# Revit family: SOLID EXIT LED EMERGENCY EXIT LIGHT TWT3051WK
name_source: partatom
category: Lighting Fixtures
revit_build: Autodesk Revit 2015 (Build: 20160512_0715(x64)
units: mm (PartAtom-declared; Revit-internal decimal feet)

## types (4) — shared parameters
Color = RAL9003
Default Elevation = 1219 mm
Depth = 181 mm  [stored 0.593832 ft]
Height = 57 mm  [stored 0.187008 ft]
Manufacturer = Teknoware Oy
Material = Plastic
Model = Solid Exit
Product Code = TWT3051WK
Viewing Distance = 30000 mm  [stored 98.4252 ft]
Width = 371 mm  [stored 1.21719 ft]

## per-type parameters (varying)
| type | Down | Left | Pictogram | Right | Type Comments | Up |
| -arrow down | Yes | No | Teknoware Pictogram PB3003E | No | PB3003E | No |
| -arrow up | No | No | Teknoware Pictogram PB3005E | No | PB3005E | Yes |
| -arrow left | No | Yes | Teknoware Pictogram PB3001E | No | PB3001E | No |
| -arrow right | No | No | Teknoware Pictogram PB3002E | Yes | PB3002E | No |

note: [stored X ft] marks values corroborated as IEEE doubles in the binary element streams (Revit-internal decimal feet)

## geometry (parser evidence)
native form markers: Blend x8, Sweep x9
no freeform markers — native parametric forms only
